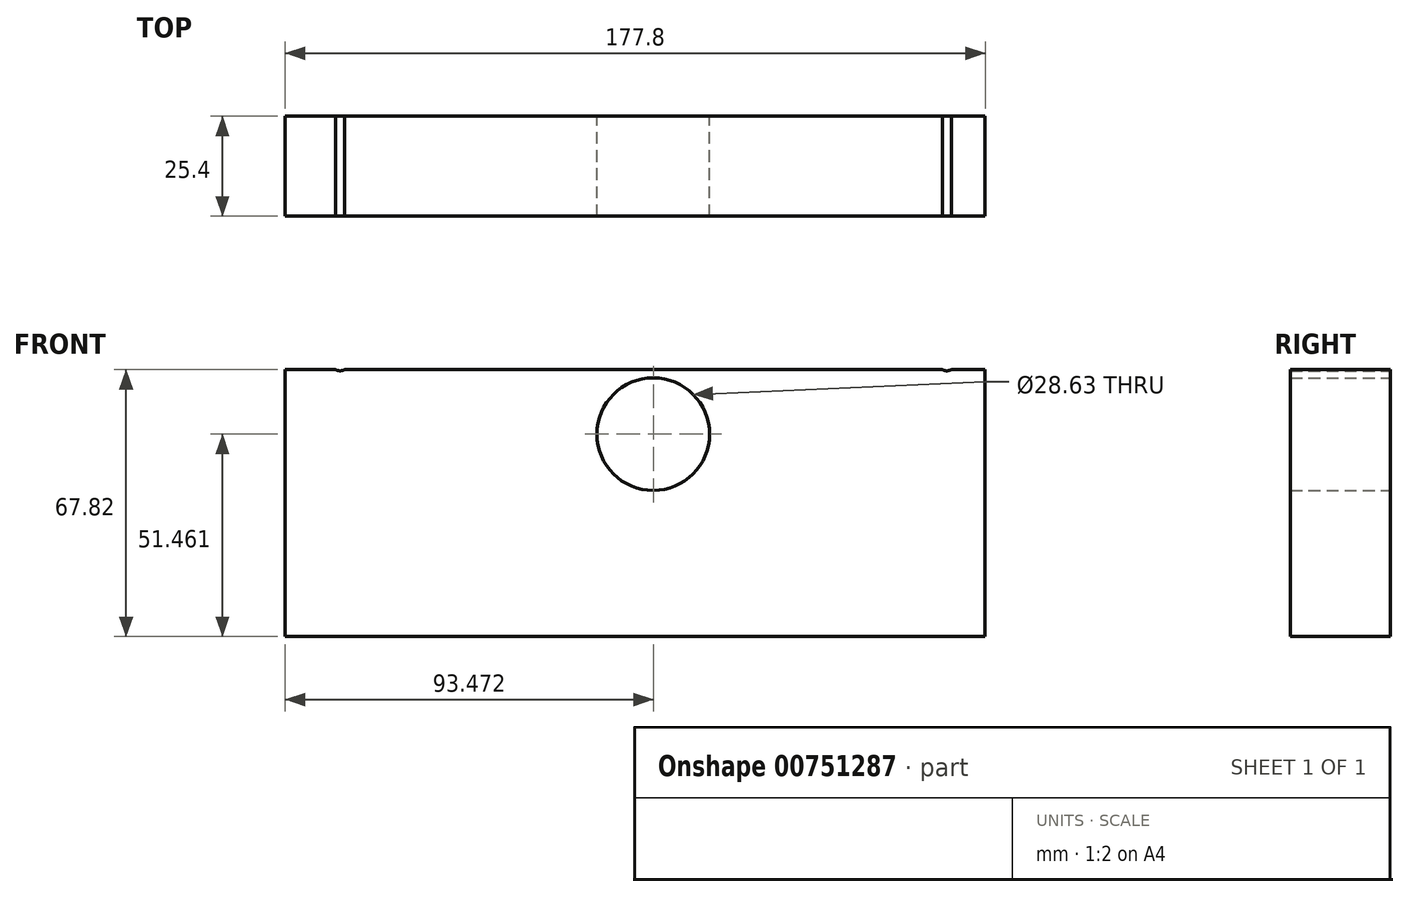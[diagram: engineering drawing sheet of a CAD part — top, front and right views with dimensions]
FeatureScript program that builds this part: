
annotation { "Feature Type Name" : "Feature", "Feature Type Description" : "" }
export const myFeature = defineFeature(function(context is Context, id is Id, definition is map)
    precondition{}
    {
        {
            var Q0;
            Q0=qCreatedBy(makeId("Front.planeOp"),FACE);
            var sketch = newSketch(context, id + "F0", { "sketchPlane" : qUnion([Q0])});
            skLineSegment(sketch, "E0.bottom", {"start": v(-51.2, 39.15) * mm, "end": v(126.6, 39.15) * mm});
            skLineSegment(sketch, "E0.top", {"start": v(-51.2, -28.67) * mm, "end": v(126.6, -28.67) * mm});
            skLineSegment(sketch, "E0.left", {"start": v(-51.2, 39.15) * mm, "end": v(-51.2, -28.67) * mm});
            skLineSegment(sketch, "E0.right", {"start": v(126.6, 39.15) * mm, "end": v(126.6, -28.67) * mm});
            skCircle(sketch, "E1", {"center": v(42.27, 22.8) * mm, "radius": 14.31 * mm});
            skCircle(sketch, "E2", {"center": v(116.84, 41.41) * mm, "radius": 2.54 * mm});
            skCircle(sketch, "E3", {"center": v(-37.3, 41.41) * mm, "radius": 2.54 * mm});
            skSolve(sketch);
        }
        {
            var Q0;
            Q0=makeQuery(id+"F0.imprint","IMPRINT",FACE,{"disambiguationData":[TD([[makeQuery(id+"F0.imprint","IMPRINT",EDGE,{"derivedFrom":sQuery(id+"F0.wireOp",EDGE,"E0.bottom")}),-1.0]])]});
            extrude(context, id + "F1", {"entities" : qUnion([Q0]), "depth" : 25.4 * mm, "offsetDistance" : 25.4 * mm});
        }
    });
